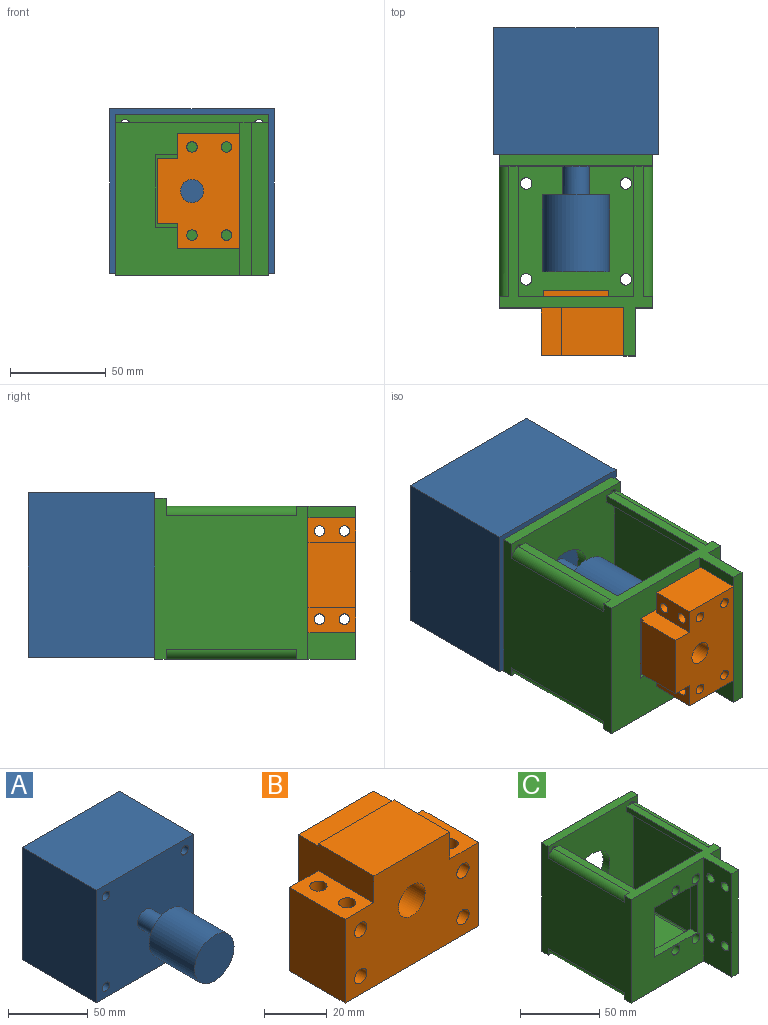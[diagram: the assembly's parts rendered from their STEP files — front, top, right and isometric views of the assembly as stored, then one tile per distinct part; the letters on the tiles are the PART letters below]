
ASSEMBLY  parts=3 mates=3
PART A: 14 faces, bbox 86x127x86 mm
  f0: cylinder r=7mm len=21mm, axis (0,1,0), area 923.6mm2, adj f10,f13
  f1: plane 86x66mm, normal (1,0,0), area 5676mm2, adj f2,f7,f9,f10
  f2: plane 86x66mm, normal (0,0,1), area 5676mm2, adj f1,f3,f9,f10
  f3: plane 86x66mm, normal (-1,0,0), area 5676mm2, adj f2,f7,f9,f10
  f4: cylinder r=3.25mm len=66mm, axis (0,-1,0), area 1347.7mm2, adj f9,f10
  f5: cylinder r=3.25mm len=66mm, axis (0,-1,0), area 1347.7mm2, adj f9,f10
  f6: cylinder r=3.25mm len=66mm, axis (0,-1,0), area 1347.7mm2, adj f9,f10
  f7: plane 86x66mm, normal (0,0,-1), area 5676mm2, adj f1,f3,f9,f10
  f8: cylinder r=3.25mm len=66mm, axis (0,-1,0), area 1347.7mm2, adj f9,f10
  f9: plane 86x86mm, normal (0,1,0), area 7263.3mm2, adj f1,f2,f3,f4,f5,f6,f7,f8
  f10: plane 86x86mm, normal (0,-1,0), area 7109.3mm2, adj f0,f1,f2,f3,f4,f5,f6,f7
  f11: cylinder r=17.5mm len=40mm, axis (0,1,0), area 4398.2mm2, adj f12,f13
  f12: plane 35x35mm, normal (0,-1,0), area 962.1mm2, adj f11
  f13: plane 35x35mm, normal (0,1,0), area 808.2mm2, adj f0,f11
PART B: 39 faces, bbox 60x34x43 mm
  f0: plane 60x32.5mm, normal (0,1,0), area 1022mm2, adj f5,f6,f7,f9,f10,f11,f12,f16
  f1: cylinder r=2.75mm len=6mm, axis (0,-1,0), area 73.4mm2, adj f15,f24,f32
  f2: cylinder r=2.75mm len=6mm, axis (0,-1,0), area 73.4mm2, adj f15,f23,f31
  f3: cylinder r=2.75mm len=6mm, axis (0,-1,0), area 73.4mm2, adj f15,f24,f26
  f4: cylinder r=2.75mm len=6mm, axis (0,-1,0), area 73.4mm2, adj f15,f22,f23
  f5: plane 32.5x25mm, normal (1,0,0), area 812.5mm2, adj f0,f6,f12,f15
  f6: plane 25x13mm, normal (0,0,1), area 277.5mm2, adj f0,f5,f7,f15,f32,f34
  f7: plane 35x34mm, normal (1,0,0), area 568.5mm2, adj f0,f6,f8,f14,f15,f36,f37,f38
  f8: plane 34x25mm, normal (0,0,1), area 850mm2, adj f7,f9,f14,f15
  f9: plane 35x34mm, normal (-1,0,0), area 568.5mm2, adj f0,f8,f10,f14,f15,f36,f37,f38
  f10: plane 25x13mm, normal (0,0,1), area 277.5mm2, adj f0,f9,f11,f15,f20,f22
  f11: plane 32.5x25mm, normal (-1,0,0), area 812.5mm2, adj f0,f10,f12,f15
  f12: plane 60x25mm, normal (0,0,-1), area 1405mm2, adj f0,f5,f11,f15,f26,f28,f30,f31
  f13: cylinder r=6mm len=34mm, axis (0,-1,0), area 1281.8mm2, adj f15,f38
  f14: plane 34x1mm, normal (0,1,0), area 34mm2, adj f7,f8,f9,f36
  f15: plane 60x43mm, normal (0,-1,0), area 2098.9mm2, adj f1,f2,f3,f4,f5,f6,f7,f8
  f16: cylinder r=2.75mm len=6mm, axis (0,-1,0), area 73.4mm2, adj f0,f27,f34
  f17: cylinder r=2.75mm len=6mm, axis (0,-1,0), area 73.4mm2, adj f0,f21,f30
  f18: cylinder r=2.75mm len=6mm, axis (0,-1,0), area 73.4mm2, adj f0,f27,f28
  f19: cylinder r=2.75mm len=6mm, axis (0,-1,0), area 73.4mm2, adj f0,f20,f21
  f20: cylinder r=2.75mm len=7.5mm, axis (0,0,1), area 99.3mm2, adj f10,f19,f35
  f21: cylinder r=2.75mm len=18mm, axis (0,0,1), area 250.5mm2, adj f17,f19,f29,f35
  f22: cylinder r=2.75mm len=7.5mm, axis (0,0,1), area 99.3mm2, adj f4,f10,f35
  f23: cylinder r=2.75mm len=18mm, axis (0,0,1), area 250.5mm2, adj f2,f4,f29,f35
  f24: cylinder r=2.75mm len=18mm, axis (0,0,1), area 250.5mm2, adj f1,f3,f25,f33
  f25: cylinder r=2.75mm len=13mm, axis (0,-1,0), area 164.1mm2, adj f24,f26,f27,f28
  f26: cylinder r=2.75mm len=7mm, axis (0,0,1), area 90.7mm2, adj f3,f12,f25
  f27: cylinder r=2.75mm len=18mm, axis (0,0,1), area 250.5mm2, adj f16,f18,f25,f33
  f28: cylinder r=2.75mm len=7mm, axis (0,0,1), area 90.7mm2, adj f12,f18,f25
  f29: cylinder r=2.75mm len=13mm, axis (0,-1,0), area 164.1mm2, adj f21,f23,f30,f31
  f30: cylinder r=2.75mm len=7mm, axis (0,0,1), area 90.7mm2, adj f12,f17,f29
  f31: cylinder r=2.75mm len=7mm, axis (0,0,1), area 90.7mm2, adj f2,f12,f29
  f32: cylinder r=2.75mm len=7.5mm, axis (0,0,1), area 99.3mm2, adj f1,f6,f33
  f33: cylinder r=2.75mm len=13mm, axis (0,-1,0), area 164.1mm2, adj f24,f27,f32,f34
  f34: cylinder r=2.75mm len=7.5mm, axis (0,0,1), area 99.3mm2, adj f6,f16,f33
  f35: cylinder r=2.75mm len=13mm, axis (0,-1,0), area 164.1mm2, adj f20,f21,f22,f23
  f36: plane 34x9mm, normal (0,0,1), area 306mm2, adj f7,f9,f14,f38
  f37: plane 34x9mm, normal (0,0,-1), area 306mm2, adj f0,f7,f9,f38
  f38: plane 34x34mm, normal (0,1,0), area 1042.9mm2, adj f7,f9,f13,f36,f37
PART C: 59 faces, bbox 80x105x84 mm
  f0: plane 80x9.05mm, normal (0,-1,0), area 724mm2, adj f1,f9,f11,f53
  f1: plane 105x80mm, normal (0,0,-1), area 5756.9mm2, adj f0,f8,f9,f13,f21,f23,f24,f31
  f2: plane 70x68mm, normal (0,0,1), area 4646.9mm2, adj f16,f17,f22,f38,f44,f45,f46,f47
  f3: plane 68x5mm, normal (0,0,-1), area 340mm2, adj f19,f22,f38,f42
  f4: plane 4.39x1.3mm, normal (0,1,0), area 4.1mm2, adj f18,f30
  f5: plane 5x3.7mm, normal (0,1,0), area 15.3mm2, adj f11,f12,f29
  f6: plane 5x3.7mm, normal (0,1,0), area 15.3mm2, adj f10,f11,f28
  f7: plane 4.39x1.3mm, normal (0,1,0), area 4.1mm2, adj f15,f27
  f8: cylinder r=5mm len=68mm, axis (0,1,0), area 534.1mm2, adj f1,f9,f24,f32
  f9: plane 84x80mm, normal (1,0,0), area 5744mm2, adj f0,f1,f8,f10,f11,f22,f24,f25
  f10: cylinder r=5mm len=68mm, axis (0,1,0), area 534.1mm2, adj f6,f9,f11,f22,f33
  f11: plane 99x80mm, normal (0,0,1), area 1310mm2, adj f0,f5,f6,f9,f10,f12,f13,f22
  f12: cylinder r=5mm len=68mm, axis (0,1,0), area 534.1mm2, adj f5,f11,f13,f22,f34
  f13: plane 84x80mm, normal (-1,0,0), area 5744mm2, adj f1,f11,f12,f21,f22,f23,f25,f31
  f14: cylinder r=1mm len=68mm, axis (0,1,0), area 106.8mm2, adj f15,f20,f22,f38
  f15: plane 70x68mm, normal (-1,0,0), area 4760mm2, adj f7,f14,f16,f22,f38
  f16: cylinder r=1mm len=68mm, axis (0,1,0), area 106.8mm2, adj f2,f15,f22,f38
  f17: cylinder r=1mm len=68mm, axis (0,1,0), area 106.8mm2, adj f2,f18,f22,f38
  f18: plane 70x68mm, normal (1,0,0), area 4760mm2, adj f4,f17,f19,f22,f38
  f19: cylinder r=1mm len=68mm, axis (0,1,0), area 106.8mm2, adj f3,f18,f22,f38
  f20: plane 68x5mm, normal (0,0,-1), area 340mm2, adj f14,f22,f38,f43
  f21: cylinder r=5mm len=68mm, axis (0,1,0), area 534.1mm2, adj f1,f13,f23,f35
  f22: plane 80x80mm, normal (0,-1,0), area 5007.1mm2, adj f2,f3,f9,f10,f11,f12,f13,f14
  f23: plane 5x5mm, normal (0,-1,0), area 5.4mm2, adj f1,f13,f21
  f24: plane 5x5mm, normal (0,-1,0), area 5.4mm2, adj f1,f8,f9
  f25: plane 80x6mm, normal (0,0,1), area 480mm2, adj f9,f13,f22,f31
  f26: cylinder r=15mm len=30mm, axis (0,1,0), area 565.5mm2, adj f22,f31
  f27: cylinder r=2.5mm len=6mm, axis (0,1,0), area 94.2mm2, adj f7,f22,f31
  f28: cylinder r=2.5mm len=6mm, axis (0,1,0), area 94.2mm2, adj f6,f22,f31
  f29: cylinder r=2.5mm len=6mm, axis (0,1,0), area 94.2mm2, adj f5,f22,f31
  f30: cylinder r=2.5mm len=6mm, axis (0,1,0), area 94.2mm2, adj f4,f22,f31
  f31: plane 84x80mm, normal (0,1,0), area 5934.6mm2, adj f1,f9,f13,f25,f26,f27,f28,f29
  f32: plane 5x5mm, normal (0,1,0), area 5.4mm2, adj f1,f8,f9
  f33: plane 5x5mm, normal (0,1,0), area 5.4mm2, adj f9,f10,f11
  f34: plane 5x5mm, normal (0,1,0), area 5.4mm2, adj f11,f12,f13
  f35: plane 5x5mm, normal (0,1,0), area 5.4mm2, adj f1,f13,f21
  f36: plane 80x64.95mm, normal (0,-1,0), area 3598.1mm2, adj f1,f11,f13,f37,f39,f40,f41,f48
  f37: plane 38x6mm, normal (0,0,1), area 228mm2, adj f36,f38,f39,f40
  f38: plane 76x72mm, normal (0,1,0), area 3825.2mm2, adj f2,f3,f11,f14,f15,f16,f17,f18
  f39: plane 38x6mm, normal (1,0,0), area 228mm2, adj f36,f37,f38,f41
  f40: plane 38x6mm, normal (-1,0,0), area 228mm2, adj f36,f37,f38,f41
  f41: plane 38x6mm, normal (0,0,-1), area 228mm2, adj f36,f38,f39,f40
  f42: plane 68x4mm, normal (1,0,0), area 272mm2, adj f3,f11,f22,f38
  f43: plane 68x4mm, normal (-1,0,0), area 272mm2, adj f11,f20,f22,f38
  f44: cylinder r=3mm len=6mm, axis (0,0,1), area 75.4mm2, adj f1,f2
  f45: cylinder r=3mm len=6mm, axis (0,0,1), area 75.4mm2, adj f1,f2
  f46: cylinder r=3mm len=6mm, axis (0,0,1), area 75.4mm2, adj f1,f2
  f47: cylinder r=3mm len=6mm, axis (0,0,1), area 75.4mm2, adj f1,f2
  f48: cylinder r=3.5mm len=7mm, axis (0,-1,0), area 131.9mm2, adj f36,f38
  f49: cylinder r=3.5mm len=7mm, axis (0,-1,0), area 131.9mm2, adj f36,f38
  f50: cylinder r=3.5mm len=7mm, axis (0,-1,0), area 131.9mm2, adj f36,f38
  f51: cylinder r=3.5mm len=7mm, axis (0,-1,0), area 131.9mm2, adj f36,f38
  f52: plane 80x25mm, normal (-1,0,0), area 1867.3mm2, adj f1,f11,f36,f54,f55,f56,f57,f58
  f53: plane 80x25mm, normal (1,0,0), area 1867.3mm2, adj f0,f1,f11,f54,f55,f56,f57,f58
  f54: plane 80x6mm, normal (0,-1,0), area 480mm2, adj f1,f11,f52,f53
  f55: cylinder r=3.25mm len=6.5mm, axis (-1,0,0), area 122.5mm2, adj f52,f53
  f56: cylinder r=3.25mm len=6.5mm, axis (-1,0,0), area 122.5mm2, adj f52,f53
  f57: cylinder r=3.25mm len=6.5mm, axis (-1,0,0), area 122.5mm2, adj f52,f53
  f58: cylinder r=3.25mm len=6.5mm, axis (-1,0,0), area 122.5mm2, adj f52,f53
PLACE A t=(-118.04,-75.37,-65.83)mm
PLACE B rot(axis=(0,-1,0),90deg) t=(-114.54,-180.37,-65.83)mm
PLACE C t=(-118.04,-75.37,-65.83)mm
MATE planar B.f0 <-> C.f36  axis (0,1,0) through (-109.29,-155.37,-95.83)mm
MATE fastened A.f0 <-> C.f26  axis (0,-1,0) through (-118.04,-75.37,-65.83)mm
MATE slider B.f13 <-> A.f11  axis (0,-1,0) through (-118.04,-146.37,-65.83)mm
